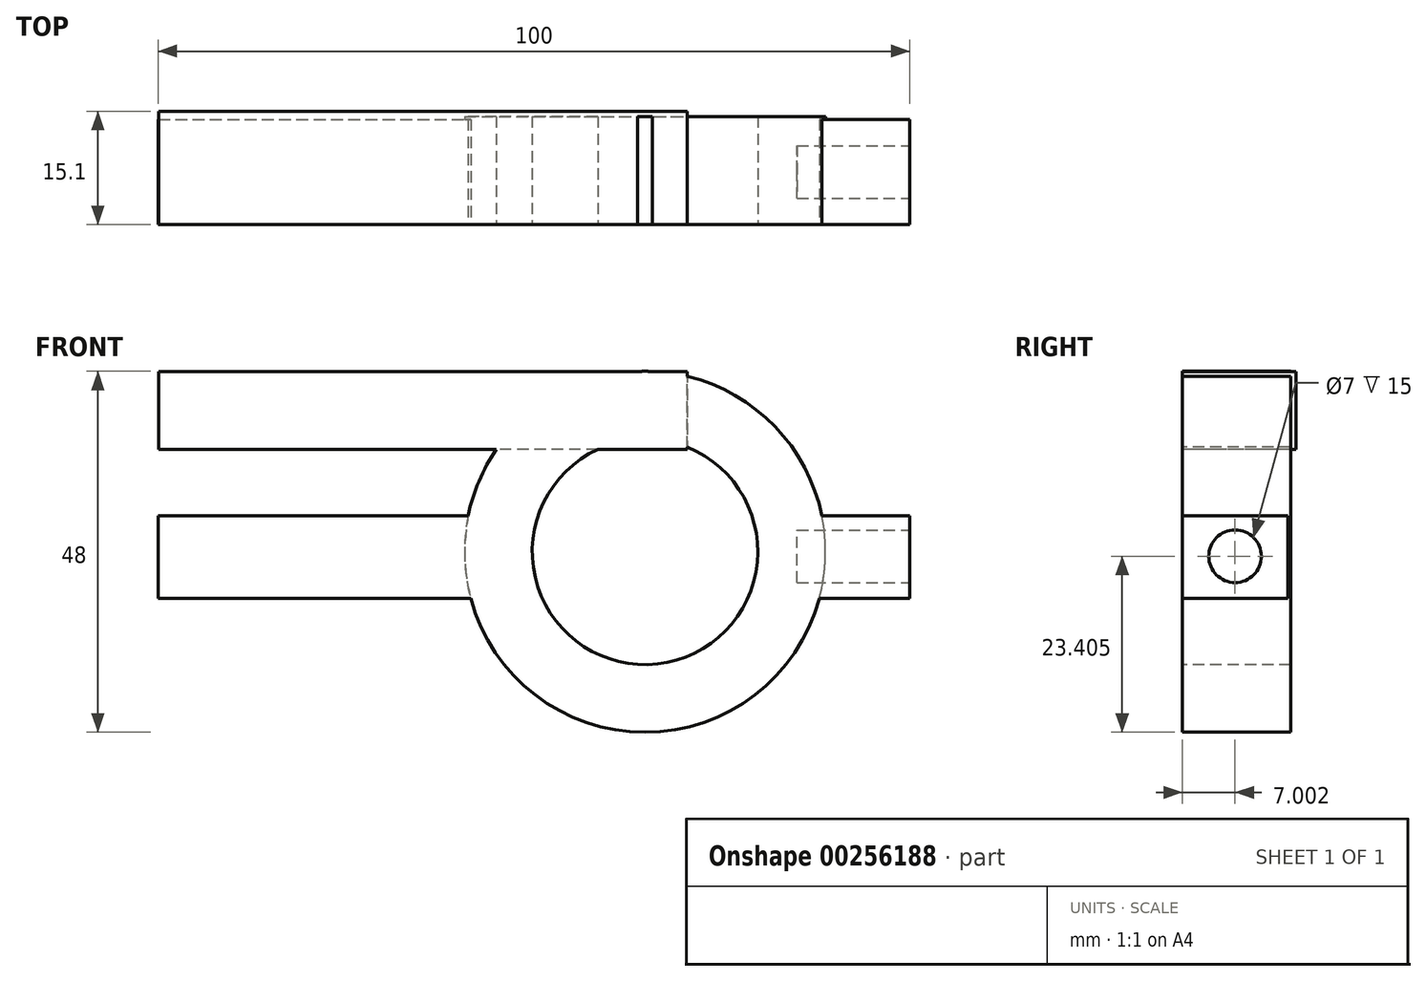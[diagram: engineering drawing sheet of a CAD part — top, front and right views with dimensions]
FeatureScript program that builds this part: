
annotation { "Feature Type Name" : "Feature", "Feature Type Description" : "" }
export const myFeature = defineFeature(function(context is Context, id is Id, definition is map)
    precondition{}
    {
        {
            var Q0;
            Q0=qCreatedBy(makeId("Top.planeOp"),FACE);
            var sketch = newSketch(context, id + "F0", { "sketchPlane" : qUnion([Q0])});
            skLineSegment(sketch, "E0.bottom", {"start": v(-70.4, 1.86) * mm, "end": v(29.6, 1.86) * mm});
            skLineSegment(sketch, "E0.top", {"start": v(-70.4, -12.14) * mm, "end": v(29.6, -12.14) * mm});
            skLineSegment(sketch, "E0.left", {"start": v(-70.4, 1.86) * mm, "end": v(-70.4, -12.14) * mm});
            skLineSegment(sketch, "E0.right", {"start": v(29.6, 1.86) * mm, "end": v(29.6, -12.14) * mm});
            skSolve(sketch);
        }
        {
            var Q0;
            Q0 = qSketchRegion(id + "F0", true);
            extrude(context, id + "F1", {"entities" : qUnion([Q0]), "depth" : 11 * mm});
        }
        {
            var Q0;
            Q0=makeQuery(id+"F1.opExtrude","SWEPT_FACE",FACE,{"disambiguationData":[OSD([sQuery(id+"F0.wireOp",EDGE,"E0.top")])]});
            var sketch = newSketch(context, id + "F2", { "sketchPlane" : qUnion([Q0])});
            skCircle(sketch, "E1", {"center": v(-5.63, 6.22) * mm, "radius": 24 * mm});
            skSolve(sketch);
        }
        {
            var Q0;
            Q0 = qSketchRegion(id + "F2", true);
            extrude(context, id + "F3", {"entities" : qUnion([Q0]), "operationType" : NewBodyOperationType.ADD, "oppositeDirection" : true, "depth" : 14.4 * mm});
        }
        {
            var Q0;
            Q0=makeQuery(id+"F3.boolean.opBoolean","MERGE",FACE,{"derivedFrom":[makeQuery(id+"F1.opExtrude","SWEPT_FACE",FACE,{"disambiguationData":[OSD([sQuery(id+"F0.wireOp",EDGE,"E0.top")])]}),makeQuery(id+"F3.opExtrude","CAP_FACE",FACE,{"disambiguationData":[OSD([sQuery(id+"F2.wireOp",EDGE,"E1")])],"isStart":true})]});
            var sketch = newSketch(context, id + "F4", { "sketchPlane" : qUnion([Q0])});
            skCircle(sketch, "E2", {"center": v(-5.63, 6.22) * mm, "radius": 15 * mm});
            skSolve(sketch);
        }
        {
            var Q0;
            Q0 = qSketchRegion(id + "F4", true);
            extrude(context, id + "F5", {"entities" : qUnion([Q0]), "operationType" : NewBodyOperationType.REMOVE, "oppositeDirection" : true, "depth" : 25 * mm});
        }
        {
            var Q0;
            Q0=makeQuery(id+"F1.opExtrude","SWEPT_FACE",FACE,{"disambiguationData":[OSD([sQuery(id+"F0.wireOp",EDGE,"E0.right")])]});
            var sketch = newSketch(context, id + "F6", { "sketchPlane" : qUnion([Q0])});
            skCircle(sketch, "E3", {"center": v(-5.14, 5.63) * mm, "radius": 3.5 * mm});
            skPoint(sketch, "E3.centerSnap0", {"position": v(-5.14, 0) * mm});
            skSolve(sketch);
        }
        {
            var Q0;
            Q0 = qSketchRegion(id + "F6", true);
            extrude(context, id + "F7", {"entities" : qUnion([Q0]), "operationType" : NewBodyOperationType.REMOVE, "oppositeDirection" : true, "depth" : 15 * mm});
        }
        {
            var Q0;
            Q0=qCreatedBy(makeId("Right.planeOp"),FACE);
            var sketch = newSketch(context, id + "F8", { "sketchPlane" : qUnion([Q0])});
            skLineSegment(sketch, "E4.bottom", {"start": v(2.96, 30.2) * mm, "end": v(-12.14, 30.2) * mm});
            skLineSegment(sketch, "E4.top", {"start": v(2.96, 19.84) * mm, "end": v(-12.14, 19.84) * mm});
            skLineSegment(sketch, "E4.left", {"start": v(2.96, 30.2) * mm, "end": v(2.96, 19.84) * mm});
            skLineSegment(sketch, "E4.right", {"start": v(-12.14, 30.2) * mm, "end": v(-12.14, 19.84) * mm});
            skSolve(sketch);
        }
        {
            var Q0;
            Q0 = qSketchRegion(id + "F8", true);
            extrude(context, id + "F9", {"entities" : qUnion([Q0]), "operationType" : NewBodyOperationType.ADD, "oppositeDirection" : true, "depth" : 70.3 * mm});
        }
    });
